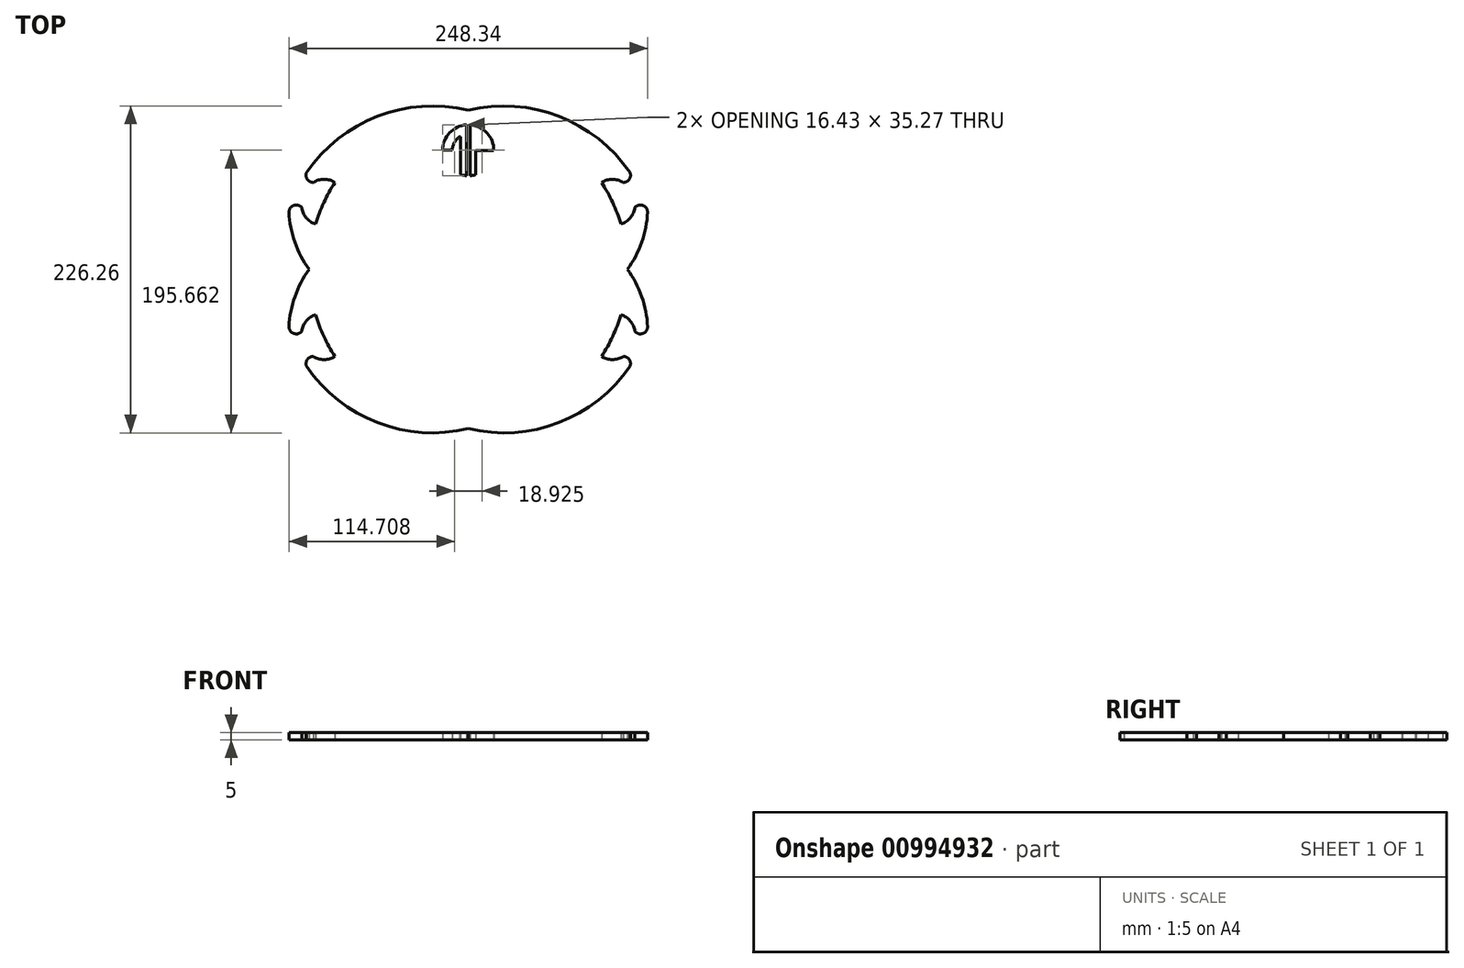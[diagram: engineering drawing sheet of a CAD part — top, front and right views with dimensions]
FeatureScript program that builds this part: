
annotation { "Feature Type Name" : "Feature", "Feature Type Description" : "" }
export const myFeature = defineFeature(function(context is Context, id is Id, definition is map)
    precondition{}
    {
        {
            var Q0;
            Q0=qCreatedBy(makeId("Top.planeOp"),FACE);
            var sketch = newSketch(context, id + "F0", { "sketchPlane" : qUnion([Q0])});
            skPoint(sketch, "E0.visualSharp", {"position": v(120, -79.79) * mm});
            skArc(sketch, "E0.filletArc", {"start": v(115, -79.79) * mm, "mid": v(118.54, -78.32) * mm, "end": v(120, -74.79) * mm});
            skArc(sketch, "E1.filletArc", {"start": v(-110.6, 69) * mm, "mid": v(-112.02, 63.47) * mm, "end": v(-107.33, 60.21) * mm});
            skArc(sketch, "E2.filletArc", {"start": v(107.33, 60.21) * mm, "mid": v(112.02, 63.47) * mm, "end": v(110.6, 69) * mm});
            skPoint(sketch, "E3.orphan", {"position": v(0, 110.21) * mm});
            skLineSegment(sketch, "E4", {"start": v(5.25, 82.22) * mm, "end": v(5.25, 65.65) * mm});
            skArc(sketch, "E5", {"start": v(-1.25, 100.17) * mm, "mid": v(-12.93, 94.58) * mm, "end": v(-17.68, 82.54) * mm});
            skArc(sketch, "E6", {"start": v(-5.25, 92.2) * mm, "mid": v(-9.45, 88.16) * mm, "end": v(-11, 82.54) * mm});
            skLineSegment(sketch, "E7", {"start": v(-17.68, 82.54) * mm, "end": v(-11, 82.54) * mm});
            skPoint(sketch, "E8.startSnap0", {"position": v(5.25, 82.22) * mm});
            skLineSegment(sketch, "E9", {"start": v(-1.25, 65.03) * mm, "end": v(-1.25, 82.54) * mm});
            skLineSegment(sketch, "E10", {"start": v(1.25, 65.03) * mm, "end": v(1.25, 82.53) * mm});
            skLineSegment(sketch, "E11", {"start": v(-1.25, 65.03) * mm, "end": v(-1.25, 100.17) * mm});
            skLineSegment(sketch, "E12", {"start": v(1.25, 65.03) * mm, "end": v(1.25, 100.17) * mm});
            skArc(sketch, "E13.trimOffspring", {"start": v(17.68, 82.22) * mm, "mid": v(13.04, 94.47) * mm, "end": v(1.25, 100.17) * mm});
            skLineSegment(sketch, "E14", {"start": v(-1.25, 100.17) * mm, "end": v(-1.25, 82.54) * mm});
            skLineSegment(sketch, "E15", {"start": v(1.25, 100.17) * mm, "end": v(1.25, 64.9) * mm});
            skPoint(sketch, "E16.start.orphan", {"position": v(0, 65.03) * mm});
            skArc(sketch, "E17.trimOffspring", {"start": v(1.25, 64.9) * mm, "mid": v(3.27, 65.16) * mm, "end": v(5.25, 65.65) * mm});
            skLineSegment(sketch, "E18", {"start": v(17.68, 82.22) * mm, "end": v(5.25, 82.22) * mm});
            skPoint(sketch, "E19.endSnap0", {"position": v(-2.76, 65.07) * mm});
            skLineSegment(sketch, "E20", {"start": v(-5.25, 65.65) * mm, "end": v(-5.25, 92.2) * mm});
            skArc(sketch, "E21", {"start": v(-5.25, 65.65) * mm, "mid": v(-3.27, 65.16) * mm, "end": v(-1.25, 64.9) * mm});
            skLineSegment(sketch, "E22.trimOffspring", {"start": v(-1.25, 65.03) * mm, "end": v(-1.25, 64.9) * mm});
            skLineSegment(sketch, "E23", {"start": v(-112.02, 66.96) * mm, "end": v(-112.02, 65.03) * mm});
            skPoint(sketch, "E23.startSnap0", {"position": v(-112.02, 63.47) * mm});
            skLineSegment(sketch, "E24", {"start": v(-49.36, 110.21) * mm, "end": v(49.36, 110.21) * mm});
            skPoint(sketch, "E24.endSnap0", {"position": v(112.02, 63.47) * mm});
            skLineSegment(sketch, "E25", {"start": v(112.02, 66.96) * mm, "end": v(112.02, 63.47) * mm});
            skArc(sketch, "E26", {"start": v(-5.25, 91.24) * mm, "mid": v(-5.54, 91.78) * mm, "end": v(-6.14, 91.66) * mm});
            skPoint(sketch, "E26.first.point", {"position": v(-6.14, 91.66) * mm});
            skPoint(sketch, "E26.second.point", {"position": v(-5.25, 91.39) * mm});
            skArc(sketch, "E27", {"start": v(0, 110.21) * mm, "mid": v(-62.75, 106.04) * mm, "end": v(-112.02, 66.96) * mm});
            skArc(sketch, "E28.MirrorCS", {"start": v(0, 110.21) * mm, "mid": v(62.75, 106.04) * mm, "end": v(112.02, 66.96) * mm});
            skArc(sketch, "E29.MirrorCS", {"start": v(0, -110.21) * mm, "mid": v(-62.75, -106.04) * mm, "end": v(-112.02, -66.96) * mm});
            skArc(sketch, "E30.MirrorCS", {"start": v(0, -110.21) * mm, "mid": v(62.75, -106.04) * mm, "end": v(112.02, -66.96) * mm});
            skArc(sketch, "E31.MirrorCS", {"start": v(-110.6, -69) * mm, "mid": v(-112.02, -63.47) * mm, "end": v(-107.33, -60.21) * mm});
            skArc(sketch, "E32.MirrorCS", {"start": v(107.33, -60.21) * mm, "mid": v(112.02, -63.47) * mm, "end": v(110.6, -69) * mm});
            skPoint(sketch, "E33.MirrorCS.end.orphan", {"position": v(-107.33, -60.21) * mm});
            skPoint(sketch, "E34.MirrorCS.end.orphan", {"position": v(107.33, -60.21) * mm});
            skArc(sketch, "E35", {"start": v(-92.3, 60.21) * mm, "mid": v(-110.21, 0) * mm, "end": v(-92.3, -60.21) * mm});
            skArc(sketch, "E36", {"start": v(-107.33, -60.21) * mm, "mid": v(-99.82, -62.44) * mm, "end": v(-92.3, -60.21) * mm});
            skArc(sketch, "E37.MirrorCS", {"start": v(-107.33, 60.21) * mm, "mid": v(-99.82, 62.44) * mm, "end": v(-92.3, 60.21) * mm});
            skArc(sketch, "E38.MirrorCS", {"start": v(107.33, 60.21) * mm, "mid": v(99.82, 62.44) * mm, "end": v(92.3, 60.21) * mm});
            skArc(sketch, "E39.MirrorCS", {"start": v(107.33, -60.21) * mm, "mid": v(99.82, -62.44) * mm, "end": v(92.3, -60.21) * mm});
            skArc(sketch, "E40.trimOffspring", {"start": v(92.3, -60.21) * mm, "mid": v(110.21, 0) * mm, "end": v(92.3, 60.21) * mm});
            skLineSegment(sketch, "E41", {"start": v(0, 0) * mm, "end": v(-110.21, 0) * mm});
            skLineSegment(sketch, "E42", {"start": v(0, 0) * mm, "end": v(-92.3, 60.21) * mm});
            skLineSegment(sketch, "E43", {"start": v(0, 0) * mm, "end": v(-105.64, 31.4) * mm});
            skLineSegment(sketch, "E44", {"start": v(0, 0) * mm, "end": v(-100.02, 46.3) * mm});
            skArc(sketch, "E45.MirrorCS", {"start": v(-115.36, 42.86) * mm, "mid": v(-112.2, 35.69) * mm, "end": v(-105.64, 31.4) * mm});
            skArc(sketch, "E46.MirrorCS", {"start": v(-124.17, 39.67) * mm, "mid": v(-120.87, 44.33) * mm, "end": v(-115.36, 42.86) * mm});
            skPoint(sketch, "E47.orphan", {"position": v(-123.54, 42.07) * mm});
            skLineSegment(sketch, "E48", {"start": v(0, 0) * mm, "end": v(-109.06, 15.87) * mm});
            skArc(sketch, "E49.MirrorCS", {"start": v(-124.17, -39.67) * mm, "mid": v(-120.87, -44.33) * mm, "end": v(-115.36, -42.86) * mm});
            skArc(sketch, "E50.MirrorCS", {"start": v(-115.36, -42.86) * mm, "mid": v(-112.2, -35.69) * mm, "end": v(-105.64, -31.4) * mm});
            skArc(sketch, "E51.MirrorCS", {"start": v(115.36, 42.86) * mm, "mid": v(112.2, 35.69) * mm, "end": v(105.64, 31.4) * mm});
            skArc(sketch, "E52.MirrorCS", {"start": v(124.17, 39.67) * mm, "mid": v(120.87, 44.33) * mm, "end": v(115.36, 42.86) * mm});
            skArc(sketch, "E53.MirrorCS", {"start": v(115.36, -42.86) * mm, "mid": v(112.2, -35.69) * mm, "end": v(105.64, -31.4) * mm});
            skArc(sketch, "E54.MirrorCS", {"start": v(124.17, -39.67) * mm, "mid": v(120.87, -44.33) * mm, "end": v(115.36, -42.86) * mm});
            skPoint(sketch, "E55.MirrorCS.end.orphan", {"position": v(-109.06, -15.87) * mm});
            skPoint(sketch, "E55.MirrorCS.start.orphan", {"position": v(-124.17, -39.67) * mm});
            skPoint(sketch, "E56.third.point", {"position": v(-120.87, -65.21) * mm});
            skPoint(sketch, "E56.third.point.positionSnap0", {"position": v(-120.87, -44.33) * mm});
            skPoint(sketch, "E57.MirrorCS.start.orphan", {"position": v(-84.02, -71.32) * mm});
            skPoint(sketch, "E58.MirrorCS.end.orphan", {"position": v(109.06, 15.87) * mm});
            skPoint(sketch, "E58.MirrorCS.start.orphan", {"position": v(124.17, 39.67) * mm});
            skPoint(sketch, "E59.MirrorCS.end.orphan", {"position": v(109.06, -15.87) * mm});
            skPoint(sketch, "E59.MirrorCS.start.orphan", {"position": v(124.17, -39.67) * mm});
            skArc(sketch, "E60.MirrorCS", {"start": v(110.21, 0) * mm, "mid": v(120.1, 18.81) * mm, "end": v(124.17, 39.67) * mm});
            skArc(sketch, "E61.MirrorCS", {"start": v(110.21, 0) * mm, "mid": v(120.1, -18.81) * mm, "end": v(124.17, -39.67) * mm});
            skPoint(sketch, "E62.MirrorCS.end.orphan", {"position": v(-124.17, 39.67) * mm});
            skPoint(sketch, "E62.MirrorCS.start.orphan", {"position": v(-110.21, 0) * mm});
            skArc(sketch, "E63.MirrorCS", {"start": v(-110.21, 0) * mm, "mid": v(-120.1, 18.81) * mm, "end": v(-124.17, 39.67) * mm});
            skArc(sketch, "E64.MirrorCS", {"start": v(-110.21, 0) * mm, "mid": v(-120.1, -18.81) * mm, "end": v(-124.17, -39.67) * mm});
            skSolve(sketch);
        }
        {
            var Q0;
            Q0=qSketchRegion(id+"F0",true);
            extrude(context, id + "F1", {"entities" : qUnion([Q0]), "depth" : 5 * mm, "offsetDistance" : 25 * mm});
        }
    });
